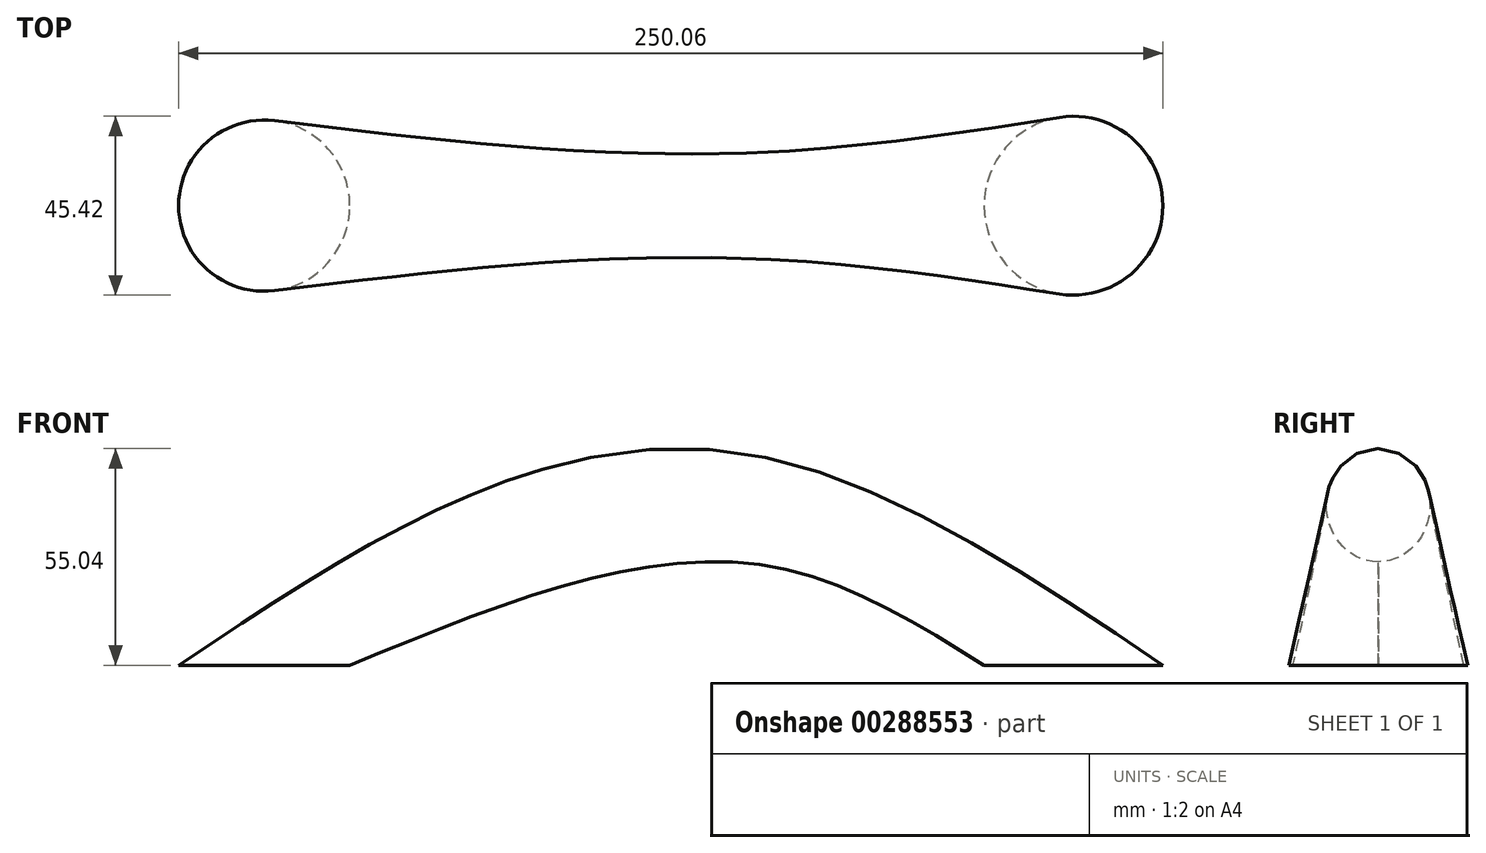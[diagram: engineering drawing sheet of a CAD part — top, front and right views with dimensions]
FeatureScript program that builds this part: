
annotation { "Feature Type Name" : "Feature", "Feature Type Description" : "" }
export const myFeature = defineFeature(function(context is Context, id is Id, definition is map)
    precondition{}
    {
        {
            var Q0;
            Q0=qCreatedBy(makeId("Front.planeOp"),FACE);
            var sketch = newSketch(context, id + "F0", { "sketchPlane" : qUnion([Q0])});
            skCircle(sketch, "E0", {"center": v(0, 0) * mm, "radius": 36.7 * mm});
            skSolve(sketch);
        }
        {
            var Q0;
            Q0=makeQuery(id+"F0.imprint","IMPRINT",FACE,{"disambiguationData":[TD([[makeQuery(id+"F0.imprint","IMPRINT",EDGE,{"derivedFrom":sQuery(id+"F0.wireOp",EDGE,"E0")}),1.0]])]});
            extrude(context, id + "F1", {"entities" : qUnion([Q0]), "depth" : 25.4 * mm});
        }
        {
            var Q0;
            Q0=makeQuery(id+"F1.opExtrude","CAP_FACE",FACE,{"disambiguationData":[OSD([sQuery(id+"F0.wireOp",EDGE,"E0")])],"isStart":false});
            cPlane(context, id + "F2", {"entities" : qUnion([Q0]), "cplaneType" : CPlaneType.OFFSET, "offset" : 25.4 * mm, "width" : 152.4 * mm, "height" : 152.4 * mm});
        }
        {
            var Q0;
            Q0=qCreatedBy(id+"F2.planeOp",FACE);
            var sketch = newSketch(context, id + "F3", { "sketchPlane" : qUnion([Q0])});
            skLineSegment(sketch, "E1", {"start": v(-9.97, 35.59) * mm, "end": v(11.3, 35.59) * mm});
            skLineSegment(sketch, "E2", {"start": v(11.3, 35.59) * mm, "end": v(0, 52.89) * mm});
            skLineSegment(sketch, "E3", {"start": v(0, 52.89) * mm, "end": v(-9.97, 35.59) * mm});
            skSolve(sketch);
        }
        {
            var Q0;
            Q0 = qSketchRegion(id + "F3", true);
            extrude(context, id + "F4", {"entities" : qUnion([Q0]), "operationType" : NewBodyOperationType.ADD, "oppositeDirection" : true, "depth" : 50.8 * mm});
        }
        {
            var Q0;
            Q0=makeQuery(id+"F1.opExtrude","SWEPT_BODY",BODY,{"disambiguationData":[OSD([sQuery(id+"F0.wireOp",EDGE,"E0")])]});
            deleteBodies(context, id + "F5", {"entities" : qUnion([Q0])});
        }
        {
            var Q0;
            Q0=qCreatedBy(makeId("Top.planeOp"),FACE);
            var sketch = newSketch(context, id + "F6", { "sketchPlane" : qUnion([Q0])});
            skCircle(sketch, "E4", {"center": v(-129.09, 0) * mm, "radius": 21.75 * mm});
            skCircle(sketch, "E5", {"center": v(76.51, 0) * mm, "radius": 22.71 * mm});
            skSolve(sketch);
        }
        {
            var Q0;
            Q0=qCreatedBy(makeId("Right.planeOp"),FACE);
            var sketch = newSketch(context, id + "F7", { "sketchPlane" : qUnion([Q0])});
            skCircle(sketch, "E6", {"center": v(0, 38.73) * mm, "radius": 13.69 * mm});
            skSolve(sketch);
        }
        {
            var Q0;
            Q0=makeQuery(id+"F6.imprint","IMPRINT",FACE,{"disambiguationData":[TD([[makeQuery(id+"F6.imprint","IMPRINT",EDGE,{"derivedFrom":sQuery(id+"F6.wireOp",EDGE,"E4")}),1.0]])]});
            var Q1;
            Q1=makeQuery(id+"F7.imprint","IMPRINT",FACE,{"disambiguationData":[TD([[makeQuery(id+"F7.imprint","IMPRINT",EDGE,{"derivedFrom":sQuery(id+"F7.wireOp",EDGE,"E6")}),1.0]])]});
            var Q2;
            Q2=makeQuery(id+"F6.imprint","IMPRINT",FACE,{"disambiguationData":[TD([[makeQuery(id+"F6.imprint","IMPRINT",EDGE,{"derivedFrom":sQuery(id+"F6.wireOp",EDGE,"E5")}),1.0]])]});
            loft(context, id + "F8", {"sheetProfilesArray" : [{ "sheetProfileEntities" : qUnion([Q0]) }, { "sheetProfileEntities" : qUnion([Q1]) }, { "sheetProfileEntities" : qUnion([Q2]) }]});
        }
    });
